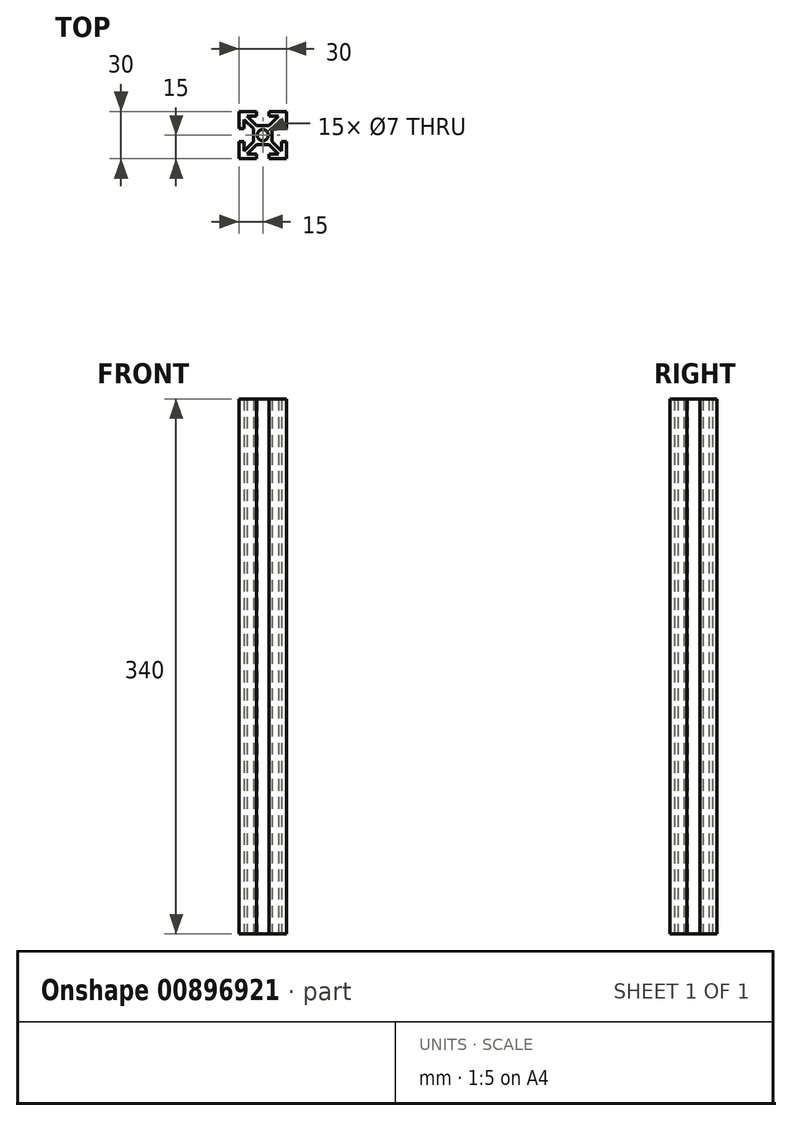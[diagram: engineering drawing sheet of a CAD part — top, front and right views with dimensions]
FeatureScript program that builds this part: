
annotation { "Feature Type Name" : "Feature", "Feature Type Description" : "" }
export const myFeature = defineFeature(function(context is Context, id is Id, definition is map)
    precondition{}
    {
        {
            var Q0;
            Q0=qCreatedBy(makeId("Top.planeOp"),FACE);
            var sketch = newSketch(context, id + "F0", { "sketchPlane" : qUnion([Q0])});
            skLineSegment(sketch, "E0", {"start": v(-15, 15) * mm, "end": v(-4, 15) * mm});
            skLineSegment(sketch, "E1", {"start": v(-4, 15) * mm, "end": v(-4, 12) * mm});
            skLineSegment(sketch, "E2", {"start": v(-4, 12) * mm, "end": v(-10, 12) * mm});
            skLineSegment(sketch, "E3", {"start": v(-10, 12) * mm, "end": v(-4, 6) * mm});
            skLineSegment(sketch, "E4", {"start": v(-4, 6) * mm, "end": v(0, 6) * mm});
            skLineSegment(sketch, "E5.MirrorCS", {"start": v(15, 15) * mm, "end": v(4, 15) * mm});
            skLineSegment(sketch, "E6.MirrorCS", {"start": v(10, 12) * mm, "end": v(4, 6) * mm});
            skLineSegment(sketch, "E7.MirrorCS", {"start": v(4, 15) * mm, "end": v(4, 12) * mm});
            skLineSegment(sketch, "E8.MirrorCS", {"start": v(4, 6) * mm, "end": v(0, 6) * mm});
            skLineSegment(sketch, "E9.MirrorCS", {"start": v(4, 12) * mm, "end": v(10, 12) * mm});
            skLineSegment(sketch, "E10.1.0", {"start": v(-6, -4) * mm, "end": v(-6, 0) * mm});
            skLineSegment(sketch, "E10.1.1", {"start": v(-12, -10) * mm, "end": v(-6, -4) * mm});
            skLineSegment(sketch, "E10.1.2", {"start": v(-15, -4) * mm, "end": v(-12, -4) * mm});
            skLineSegment(sketch, "E10.1.3", {"start": v(-12, 10) * mm, "end": v(-6, 4) * mm});
            skLineSegment(sketch, "E10.1.4", {"start": v(-6, 4) * mm, "end": v(-6, 0) * mm});
            skLineSegment(sketch, "E10.1.5", {"start": v(-15, 4) * mm, "end": v(-12, 4) * mm});
            skLineSegment(sketch, "E10.1.6", {"start": v(-12, 4) * mm, "end": v(-12, 10) * mm});
            skLineSegment(sketch, "E10.1.7", {"start": v(-15, -15) * mm, "end": v(-15, -4) * mm});
            skLineSegment(sketch, "E10.1.8", {"start": v(-15, 15) * mm, "end": v(-15, 4) * mm});
            skLineSegment(sketch, "E10.1.9", {"start": v(-12, -4) * mm, "end": v(-12, -10) * mm});
            skLineSegment(sketch, "E10.2.0", {"start": v(4, -6) * mm, "end": v(0, -6) * mm});
            skLineSegment(sketch, "E10.2.1", {"start": v(10, -12) * mm, "end": v(4, -6) * mm});
            skLineSegment(sketch, "E10.2.2", {"start": v(4, -15) * mm, "end": v(4, -12) * mm});
            skLineSegment(sketch, "E10.2.3", {"start": v(-10, -12) * mm, "end": v(-4, -6) * mm});
            skLineSegment(sketch, "E10.2.4", {"start": v(-4, -6) * mm, "end": v(0, -6) * mm});
            skLineSegment(sketch, "E10.2.5", {"start": v(-4, -15) * mm, "end": v(-4, -12) * mm});
            skLineSegment(sketch, "E10.2.6", {"start": v(-4, -12) * mm, "end": v(-10, -12) * mm});
            skLineSegment(sketch, "E10.2.7", {"start": v(15, -15) * mm, "end": v(4, -15) * mm});
            skLineSegment(sketch, "E10.2.8", {"start": v(-15, -15) * mm, "end": v(-4, -15) * mm});
            skLineSegment(sketch, "E10.2.9", {"start": v(4, -12) * mm, "end": v(10, -12) * mm});
            skLineSegment(sketch, "E10.3.0", {"start": v(6, 4) * mm, "end": v(6, 0) * mm});
            skLineSegment(sketch, "E10.3.1", {"start": v(12, 10) * mm, "end": v(6, 4) * mm});
            skLineSegment(sketch, "E10.3.2", {"start": v(15, 4) * mm, "end": v(12, 4) * mm});
            skLineSegment(sketch, "E10.3.3", {"start": v(12, -10) * mm, "end": v(6, -4) * mm});
            skLineSegment(sketch, "E10.3.4", {"start": v(6, -4) * mm, "end": v(6, 0) * mm});
            skLineSegment(sketch, "E10.3.5", {"start": v(15, -4) * mm, "end": v(12, -4) * mm});
            skLineSegment(sketch, "E10.3.6", {"start": v(12, -4) * mm, "end": v(12, -10) * mm});
            skLineSegment(sketch, "E10.3.7", {"start": v(15, 15) * mm, "end": v(15, 4) * mm});
            skLineSegment(sketch, "E10.3.8", {"start": v(15, -15) * mm, "end": v(15, -4) * mm});
            skLineSegment(sketch, "E10.3.9", {"start": v(12, 4) * mm, "end": v(12, 10) * mm});
            skPoint(sketch, "E10.center", {"position": v(0, 0) * mm});
            skCircle(sketch, "E11", {"center": v(0, 0) * mm, "radius": 3.5 * mm});
            skSolve(sketch);
        }
        {
            var Q0;
            Q0 = qSketchRegion(id + "F0", true);
            extrude(context, id + "F1", {"entities" : qUnion([Q0]), "depth" : 340 * mm, "offsetDistance" : 25 * mm});
        }
    });
